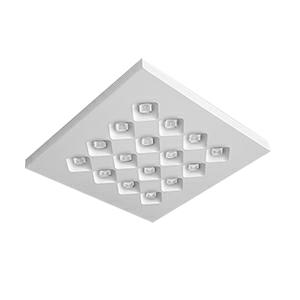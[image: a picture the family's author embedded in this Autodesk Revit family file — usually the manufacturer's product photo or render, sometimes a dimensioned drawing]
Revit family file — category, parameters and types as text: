
# Revit family: 3f_filippi_-_3f_diagon_3f_filippi_-_23030_a0686_-_3f_diagon_25w-840_dali_596x596___corn_plaf__efab
name_source: partatom
category: Lighting Fixtures
units: mm (PartAtom-declared; Revit-internal decimal feet)

## family parameters
Cut with Voids When Loaded = No
Host = Face
Light Source = No
Part Type = Normal
Room Calculation Point = No
Round Connector Dimension = Use Diameter
Shared = No

## types (1)
- 3F Filippi - 3F Dìagon (1 x LED, 4250 lm, 28 W, 4000 K)
    Apparent Load = 28 VA
    Approval mark = CE
    CIE Flux Codes = 67 96 100 100 100
    Color Rendering = 80
    Color Temperature = 4000 K
    Control Gear = Electronic transformer
    Default Elevation = 1800 mm
    Description = ILLUMINOTECHNICAL
Luminous efficiency 100% (DLOR 100%, ULOR 0%).
Initial luminous flux of the luminaire 4250 lm.
Direct symmetric distribution.
Installation Interdistance Transv.D = 1.39 x hu - Long.D = 1.39 x hu.
Average luminance <1500 cd/m² for radial angles >65°.
Tabular UGR (CIE 117 - 4H-8H; S=0.25H; 70/50/20): RUG 17.3 - 17.3.
Beam angle: 93° - 92°.
Luminous efficacy 152 lm/W.
Lifetime (L95/B10): 30000 h. (tq+25°C)
Lifetime (L90/B10): 50000 h. (tq+25°C)
Lifetime (L80/B10): 80000 h. (tq+25°C)
Lifetime (L75/B10): 100000 h. (tq+25°C)
Sudden decreased luminous flux after 50000 hours: 0% (C0).
Photobiological safety in compliance with IEC/TR 62778: RG0 risk exempt, (IEC 62471).
In compliance with IEC/EN 62722-2-1 - IEC/EN 62717 standards.

SOURCE
Squared LED module 25W/840.
Energy efficiency class (UE 2019/2020 - UE 2019/2015): C.
CIE 13.3 Colour rendering index: CRI >80 (R9 <50%).
IES TM-30 Fidelity Index: Rf = 84 Rg = 95.
CCT nominal colour temperature 4000 K.
Colour initial tolerance (MacAdam): SDCM 3.

MECHANICAL
Housing in hot-galvanised steel, painted in white polyester.
Honeycombed diagonal screen in white anti-glare polycarbonate.
Rhomboidal lenses with differentiated surfaces, etched and prismatic to optimise the orientation of the luminous flux, in transparent methacrylate (PMMA).
Luminaire with limited surface temperature. - D - (EN 60598-2-24)
Dimensions: 600x600 mm, height 40 mm. Weight 6.18 kg.
IP43 protection degree for exposed part, IP20 for recessed part.
Mechanical strength to impacts IK06 (1 joule).
Glow-wire test resistance 650°C.

ELECTRICAL
Halogen Free DALI-2 DATI (Parts 251, 252, 253), PUSH-DIM, electronic wiring 230V-50/60Hz, power factor 0.95 at full load, THD <25%, constant output current, class I, 1 driver, 1 DALI addresse.
Power of the luminaire 28 W.
ENEC - CE.
SAFE FLICKER: PstLM=<1 and SVM=<0.4 (IEC TR 61547-1 and IEC TR 63158), to ensure a more comfortable and safe light.
Luminaire compliant with EN 60598-2-22 for power supply from a centralised emergency system CPSS (Central Power Supply System), not incorporated in the luminaire - high risk areas excluded. The default power and flux are 100% in AC and 15% in DC.
Ambient temperature from 0°C to +25°C.
Temperature class T6 max 85°C.
Quick connection.
Relative humidity UR: <85%.

INSTALLATION
Ceiling.
Height only 40 mm.
All accessories dedicated to this product are available on the Catalog and on our website www.3F-Filippi.com.

ACCESSORIES
A0686 - 596x596 Diagon frame for Ceiling installation.

APPLICATIONS
Environments: staterooms, with VDTs, offices.
Environments with exacting visual tasks, where diffused soft light for optimum visual comfort is required.

LIGHT MANAGEMENT
Recommended minimum setting: 10%.
The luminaire, equipped with (DALI-2 DATI) driver, can be controlled manually with 3F Easy Dim technology or automatically/manually with wired or wireless DALI/D2D control systems.
The D2D driver guarantees interoperability with other devices with the same certification by making the following information available:
Device Data (Part 251), Energy Report (Part 252), Diagnosis & Maintenance (Part 253).
In electrical systems without a regulation system (manual or automatic) and DALI bus, a suitable jumper must be made on the DA-DA terminals of the appliance.

WARNING
Luminaire designed for disposal/recycling at end-of-life.
Replaceable (LED only) light source by a professional. Replaceable control gear by a professional.
    Height = 0 mm  [stored 0 ft]
    Lamp = 1 x LED
    Lamp Light Flux = 4250 lm
    Lamp Power = 28 W
    Lamp count = 1
    Length = 600 mm
    Lifetime = 50000 h
    Luminous efficacy = 152 lm/W
    Manufacturer = 3F Filippi
    ModVariant = No
    Model = 3F Filippi - 23030+A0686 - 3F Diagon 25W-840 DALI 596x596 + Corn.plaf.
    Mounting Place = Ceiling
    Mounting Type = Recessed
    Number of Poles = 1
    OnlyDefault = Yes
    Power Factor = 1
    Product Name = 3F Filippi - 3F Dìagon
    Product group = recessed luminaire
    ProductGroupID = 4
    Protection Class = Protection class I
    Protection Degree = IP 20
    RLX_Detail_Level = 1
    RLX_Emergency_Light_Flux = 0 lm
    RLX_Emergency_Type = 0
    RLX_Emergency_Type_DB = No
    RlxData = <blob elided: 98353 chars, md5=ab5c0a4d>
    Socket = socket
    Standby Power = 0 W
    System Light Flux = 4250 lm
    System Power = 28 W
    Type Comments = Product without accessories
    Type Image = 3ffilippi_3f_diagon__a0686.jpg
    URL = http://relux.com
    VarID = ---
    Voltage = 0 V
    Weight = 0.00 kg
    Width = 600 mm

note: [stored X ft] marks values corroborated as IEEE doubles in the binary element streams (Revit-internal decimal feet)

## geometry (parser evidence)
native form markers: Blend x4, Sweep x8
no freeform markers — native parametric forms only
